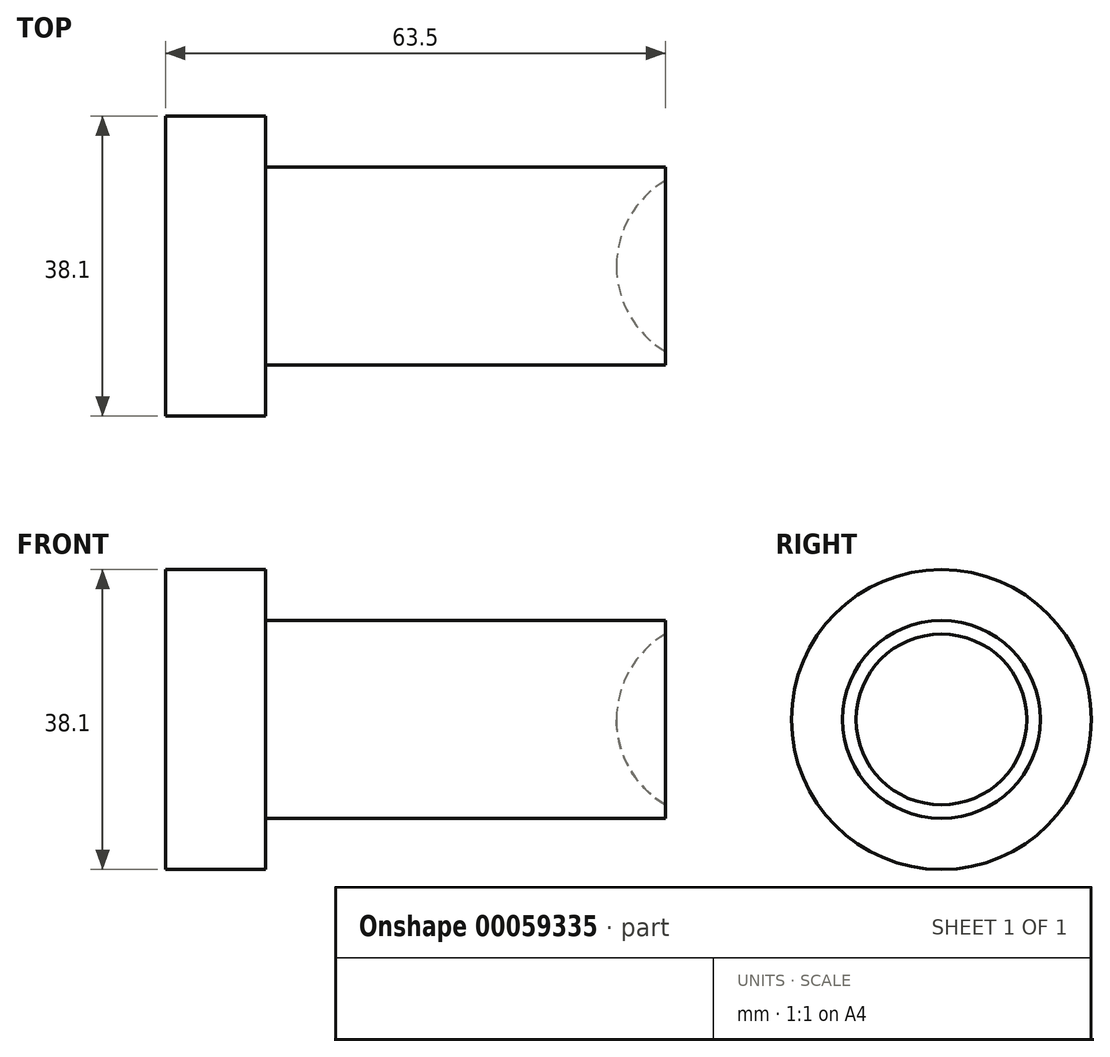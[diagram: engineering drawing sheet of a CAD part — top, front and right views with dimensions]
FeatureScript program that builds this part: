
annotation { "Feature Type Name" : "Feature", "Feature Type Description" : "" }
export const myFeature = defineFeature(function(context is Context, id is Id, definition is map)
    precondition{}
    {
        {
            var Q0;
            Q0=qCreatedBy(makeId("Right.planeOp"),FACE);
            var sketch = newSketch(context, id + "F0", { "sketchPlane" : qUnion([Q0])});
            skCircle(sketch, "E0", {"center": v(0, 0) * mm, "radius": 19.05 * mm});
            skSolve(sketch);
        }
        {
            var Q0;
            Q0 = qSketchRegion(id + "F0", true);
            extrude(context, id + "F1", {"entities" : qUnion([Q0]), "oppositeDirection" : true, "depth" : 12.7 * mm});
        }
        {
            var Q0;
            Q0=makeQuery(id+"F1.opExtrude","CAP_FACE",FACE,{"disambiguationData":[OSD([sQuery(id+"F0.wireOp",EDGE,"E0")])],"isStart":true});
            var sketch = newSketch(context, id + "F2", { "sketchPlane" : qUnion([Q0])});
            skCircle(sketch, "E1", {"center": v(0, 0) * mm, "radius": 12.57 * mm});
            skSolve(sketch);
        }
        {
            var Q0;
            Q0=makeQuery(id+"F2.imprint","IMPRINT",FACE,{"disambiguationData":[TD([[makeQuery(id+"F2.imprint","IMPRINT",EDGE,{"derivedFrom":sQuery(id+"F2.wireOp",EDGE,"E1")}),1.0]])]});
            extrude(context, id + "F3", {"entities" : qUnion([Q0]), "operationType" : NewBodyOperationType.ADD, "depth" : 50.8 * mm});
        }
        {
            var Q0;
            Q0=qCreatedBy(makeId("Front.planeOp"),FACE);
            var sketch = newSketch(context, id + "F4", { "sketchPlane" : qUnion([Q0])});
            skArc(sketch, "E2", {"start": v(69.72, 0) * mm, "mid": v(57.15, 12.57) * mm, "end": v(44.58, 0) * mm});
            skLineSegment(sketch, "E3", {"start": v(44.58, 0) * mm, "end": v(69.72, 0) * mm});
            skSolve(sketch);
        }
        {
            var Q0;
            Q0=makeQuery(id+"F4.imprint","IMPRINT",FACE,{"disambiguationData":[TD([[makeQuery(id+"F4.imprint","IMPRINT",EDGE,{"derivedFrom":sQuery(id+"F4.wireOp",EDGE,"E2")}),1.0]])]});
            var Q1;
            Q1=sQuery(id+"F4.wireOp",EDGE,"E3");
            revolve(context, id + "F5", {"operationType" : NewBodyOperationType.REMOVE, "entities" : qUnion([Q0]), "axis" : qUnion([Q1]), "revolveType" : RevolveType.FULL});
        }
    });
